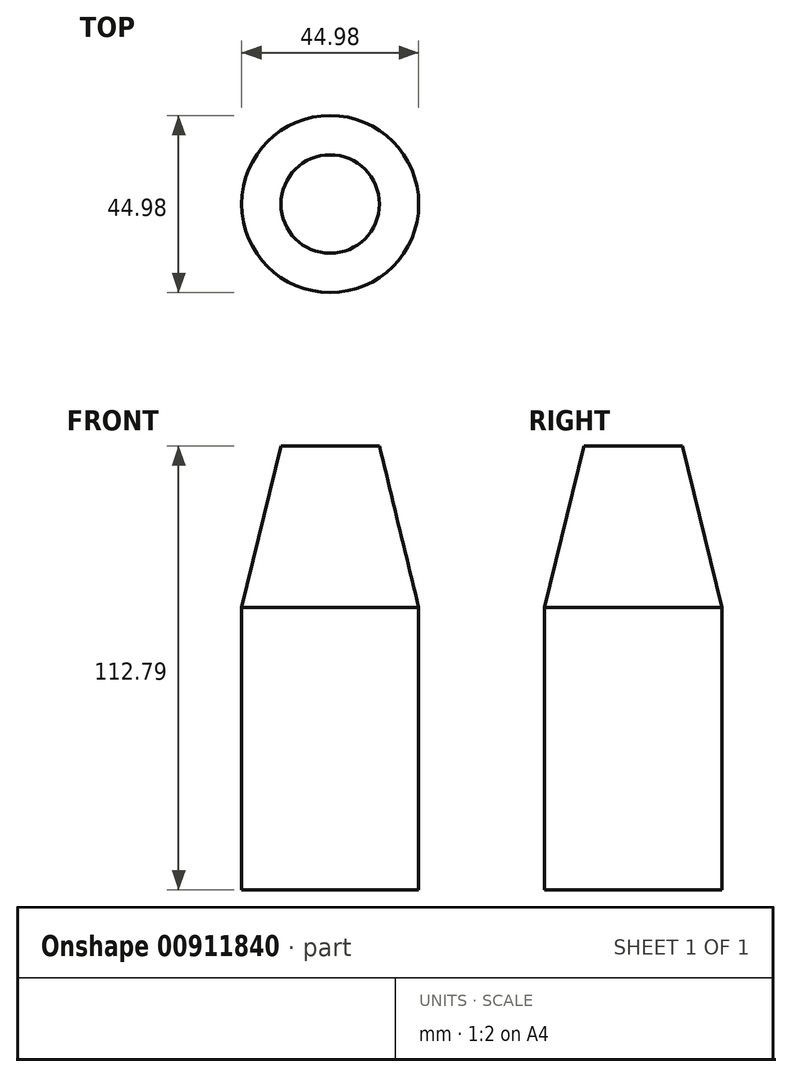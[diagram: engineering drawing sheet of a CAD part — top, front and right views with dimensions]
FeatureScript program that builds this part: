
annotation { "Feature Type Name" : "Feature", "Feature Type Description" : "" }
export const myFeature = defineFeature(function(context is Context, id is Id, definition is map)
    precondition{}
    {
        {
            var Q0;
            Q0=qCreatedBy(makeId("Front.planeOp"),FACE);
            var sketch = newSketch(context, id + "F0", { "sketchPlane" : qUnion([Q0])});
            skLineSegment(sketch, "E0.bottom", {"start": v(0, -71.74) * mm, "end": v(-22.49, -71.74) * mm});
            skLineSegment(sketch, "E0.top", {"start": v(0, 0) * mm, "end": v(-22.49, 0) * mm});
            skLineSegment(sketch, "E0.left", {"start": v(0, -71.74) * mm, "end": v(0, 0) * mm});
            skLineSegment(sketch, "E0.right", {"start": v(-22.49, -71.74) * mm, "end": v(-22.49, 0) * mm});
            skLineSegment(sketch, "E1", {"start": v(-22.49, 0) * mm, "end": v(-12.5, 41.05) * mm});
            skLineSegment(sketch, "E2", {"start": v(-12.5, 41.05) * mm, "end": v(0, 41.05) * mm});
            skLineSegment(sketch, "E3", {"start": v(0, 41.05) * mm, "end": v(0, 0) * mm});
            skLineSegment(sketch, "E4", {"start": v(0, 51.05) * mm, "end": v(0, -75.9) * mm});
            skSolve(sketch);
        }
        {
            var Q0;
            Q0 = qSketchRegion(id + "F0", true);
            var Q1;
            Q1=sQuery(id+"F0.wireOp",EDGE,"E4");
            revolve(context, id + "F1", {"surfaceOperationType" : NewSurfaceOperationType.NEW, "entities" : qUnion([Q0]), "axis" : qUnion([Q1]), "revolveType" : RevolveType.FULL});
        }
    });
